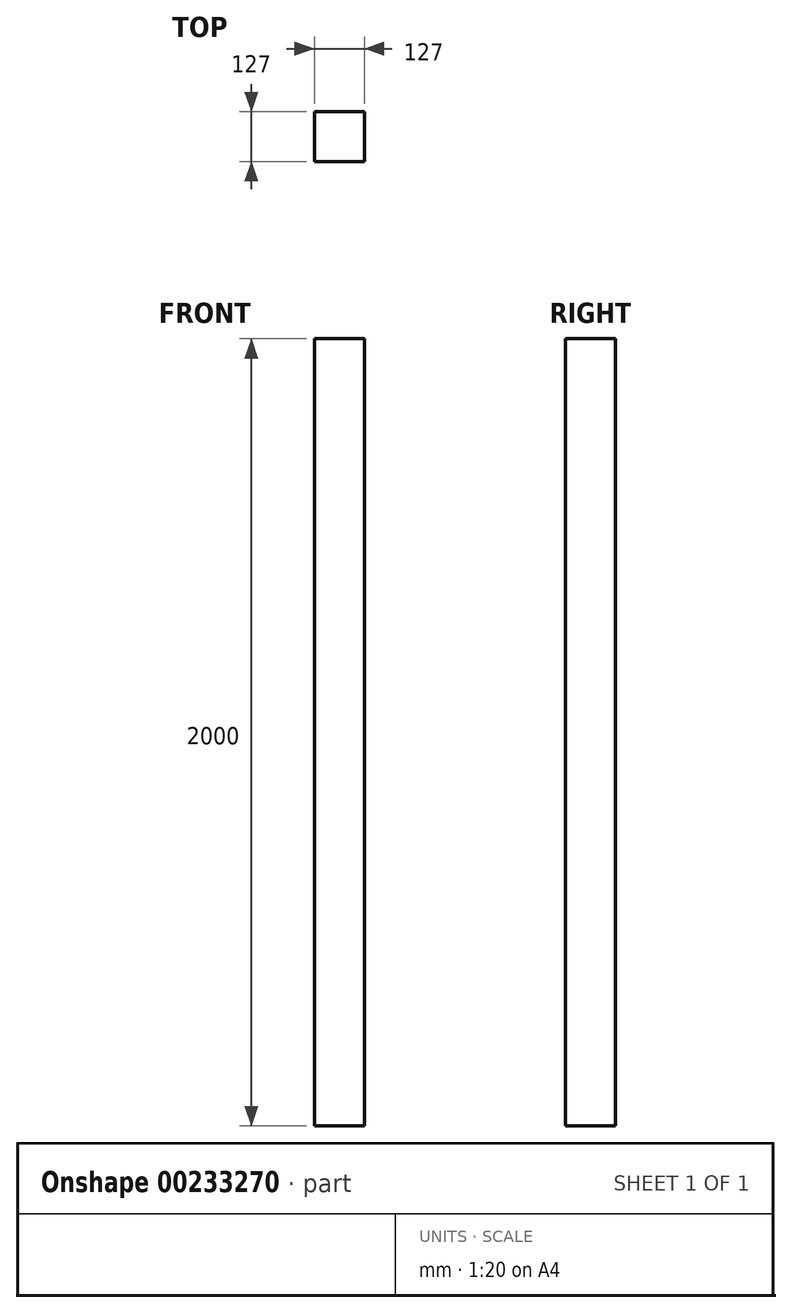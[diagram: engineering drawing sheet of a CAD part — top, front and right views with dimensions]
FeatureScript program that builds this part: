
annotation { "Feature Type Name" : "Feature", "Feature Type Description" : "" }
export const myFeature = defineFeature(function(context is Context, id is Id, definition is map)
    precondition{}
    {
        {
            var Q0;
            Q0=qCreatedBy(makeId("Front.planeOp"),FACE);
            var sketch = newSketch(context, id + "F0", { "sketchPlane" : qUnion([Q0])});
            skLineSegment(sketch, "E0.bottom", {"start": v(-958.5, 1009.42) * mm, "end": v(-831.5, 1009.42) * mm});
            skLineSegment(sketch, "E0.top", {"start": v(-958.5, -990.58) * mm, "end": v(-831.5, -990.58) * mm});
            skLineSegment(sketch, "E0.left", {"start": v(-958.5, 1009.42) * mm, "end": v(-958.5, -990.58) * mm});
            skLineSegment(sketch, "E0.right", {"start": v(-831.5, 1009.42) * mm, "end": v(-831.5, -990.58) * mm});
            skSolve(sketch);
        }
        {
            var Q0;
            Q0=makeQuery(id+"F0.imprint","IMPRINT",FACE,{"disambiguationData":[TD([[makeQuery(id+"F0.imprint","IMPRINT",EDGE,{"derivedFrom":sQuery(id+"F0.wireOp",EDGE,"E0.bottom")}),-1.0]])]});
            extrude(context, id + "F1", {"entities" : qUnion([Q0]), "depth" : 127 * mm});
        }
    });
